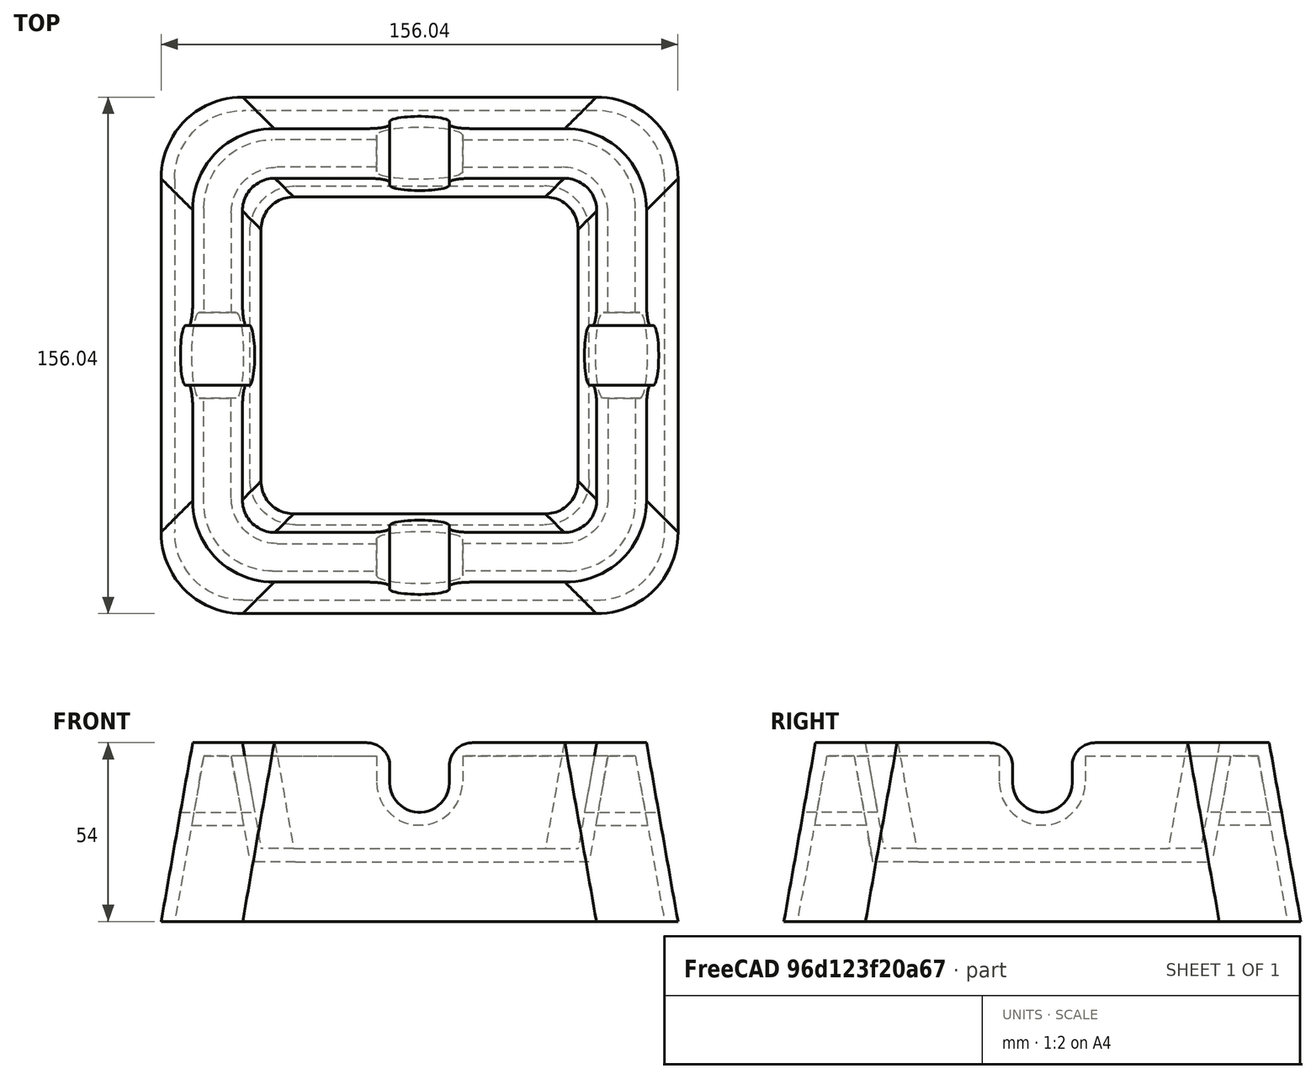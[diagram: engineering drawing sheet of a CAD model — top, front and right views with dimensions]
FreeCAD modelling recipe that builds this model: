
FCSTD DOCUMENT  (FreeCAD 1.1R42340 (Git))
Label: 25-SPO-22-BAD_IDEA
License: Creative Commons Attribution-NonCommercial-ShareAlike 4.0
LicenseURL: https://creativecommons.org/licenses/by-nc-sa/4.0/
objects: Sketcher::SketchObject×3, PartDesign::Fillet×3, PartDesign::Pocket×2, App::Point×1, PartDesign::Pad×1, PartDesign::PolarPattern×1, PartDesign::Thickness×1, PartDesign::Body×1, App::TextDocument×1
note: 30 computed .brp shape members not serialized (recipe doc carries the construction recipe); baked Part::Feature solids carry a one-line shape summary decoded from their .brp

FEATURE [App::Point] Origin001  label="Origine"
  Role = Origin
FEATURE [Sketcher::SketchObject] Sketch002
  ArcFitTolerance = 1e-06
  ExternalTypes = [0,0,0,0,0]
  FullyConstrained = true
  MakeInternals = false
  MapMode = 5
  Placement = pos=(0,0,0) rot=(1,0,0;3.14159rad)
  sketch-geometry (6):
    g0: LineSegment StartX=-68.5 StartY=68.5 StartZ=0 EndX=-68.5 EndY=-68.5 EndZ=0
    g1: LineSegment StartX=-68.5 StartY=-68.5 StartZ=0 EndX=68.5 EndY=-68.5 EndZ=0
    g2: LineSegment StartX=68.5 StartY=-68.5 StartZ=0 EndX=68.5 EndY=68.5 EndZ=0
    g3: LineSegment StartX=68.5 StartY=68.5 StartZ=0 EndX=-68.5 EndY=68.5 EndZ=0
    g4: GeomPoint [constr] X=-68.5 Y=68.5 Z=0
    g5: GeomPoint [constr] X=68.5 Y=-68.5 Z=0
  constraints (13):
    c: Vertical(g0)
    c: Vertical(g2)
    c: Horizontal(g1)
    c: Horizontal(g3)
    c: Equal(g2,g3)
    c: Coincident(g1,g2)
    c: Coincident(g1,g5)
    c: Coincident(g0,g3)
    c: Coincident(g0,g4)
    c: Coincident(g0,g1)
    c: Coincident(g2,g3)
    c: Symmetric(g0,g1,g-1)
    c: DistanceX(g1,g1) = 137
FEATURE [PartDesign::Pad] Pad
  Direction = (0,0,-1)
  Length = 54
  Length2 = 10
  Placement = pos=(0,0,0) rot=(1,0,0;3.14159rad)
  Profile = -> Sketch002
  ReferenceAxis = -> Sketch002 [N_Axis]
  Refine = true
  Suppressed = false
  TaperAngle = 10
  Type = 0
FEATURE [Sketcher::SketchObject] Sketch
  ArcFitTolerance = 1e-06
  AttachmentSupport = -> [Pad]
  ExternalGeometry = -> [Sketch002]
  ExternalTypes = [0,0]
  FullyConstrained = true
  MakeInternals = false
  MapMode = 5
  sketch-geometry (5):
    g0: LineSegment StartX=-53.5 StartY=-53.5 StartZ=0 EndX=-53.5 EndY=53.5 EndZ=0
    g1: LineSegment StartX=-53.5 StartY=53.5 StartZ=0 EndX=53.5 EndY=53.5 EndZ=0
    g2: LineSegment StartX=53.5 StartY=53.5 StartZ=0 EndX=53.5 EndY=-53.5 EndZ=0
    g3: LineSegment StartX=53.5 StartY=-53.5 StartZ=0 EndX=-53.5 EndY=-53.5 EndZ=0
    g4: LineSegment [constr] StartX=-53.5 StartY=53.5 StartZ=0 EndX=-53.5 EndY=68.5 EndZ=0
  constraints (15):
    c: Coincident(g0,g1)
    c: Coincident(g0,g3)
    c: Coincident(g1,g2)
    c: Coincident(g2,g3)
    c: Perpendicular(g4,g1)
    c: PointOnObject(g4,g1)
    c: Vertical(g4,g0)
    c: Horizontal(g3)
    c: Vertical(g0)
    c: Vertical(g2)
    c: PointOnObject(g4,g-3)
    c: Horizontal(g1)
    c: Equal(g0,g1)
    c: Symmetric(g2,g4,g-1)
    c: Distance(g4,g4) = 15
FEATURE [PartDesign::Pocket] Pocket
  BaseFeature = -> Pad
  Direction = (0,0,-1)
  Length = 32
  Length2 = 5
  Offset = -22
  Placement = pos=(0,0,0) rot=(1,0,0;3.14159rad)
  Profile = -> Sketch
  ReferenceAxis = -> Sketch [N_Axis]
  Refine = true
  Suppressed = false
  TaperAngle = -10
  Type = 0
  expr: Length = 54 - 22
FEATURE [Sketcher::SketchObject] Sketch003
  ArcFitTolerance = 1e-06
  AttachmentSupport = -> [Origin]
  ExternalTypes = [0]
  FullyConstrained = true
  MakeInternals = false
  MapMode = 5
  Placement = pos=(0,0,0) rot=(1,0,0;1.5708rad)
  sketch-geometry (4):
    g0: ArcOfCircle CenterX=0 CenterY=0 CenterZ=0 NormalX=0 NormalY=0 NormalZ=1 AngleXU=0 Radius=9 StartAngle=1e-16 EndAngle=3.14159
    g1: ArcOfCircle CenterX=-7e-16 CenterY=-12 CenterZ=0 NormalX=0 NormalY=0 NormalZ=1 AngleXU=0 Radius=9 StartAngle=3.14159 EndAngle=6.28319
    g2: LineSegment StartX=9 StartY=1.1e-15 StartZ=0 EndX=9 EndY=-12 EndZ=0
    g3: LineSegment StartX=-9 StartY=1.1e-15 StartZ=0 EndX=-9 EndY=-12 EndZ=0
  constraints (9):
    c: Tangent(g0,g2) = 1.5708
    c: Tangent(g0,g3) = -1.5708
    c: Tangent(g1,g2) = 1.5708
    c: Tangent(g1,g3) = -1.5708
    c: Equal(g0,g1)
    c: Vertical(g3)
    c: Radius(g0) = 9
    c: Coincident(g0,g-1)
    c: Distance(g1,g-1) = 12
FEATURE [PartDesign::Pocket] Pocket001
  BaseFeature = -> Pocket
  Direction = (0,1,-2e-16)
  Length = 5
  Length2 = 5
  Midplane = true
  Placement = pos=(0,0,0) rot=(1,0,0;3.14159rad)
  Profile = -> Sketch003
  ReferenceAxis = -> Sketch003 [N_Axis]
  Refine = true
  Suppressed = false
  Type = 1
FEATURE [PartDesign::PolarPattern] PolarPattern
  Angle = 90
  Axis = -> Z_Axis
  BaseFeature = -> Pocket001
  Mode = 1
  Occurrences = 2
  Offset = 90
  Originals = -> [Pocket001]
  Placement = pos=(0,0,0) rot=(1,0,0;3.14159rad)
  Refine = true
  Suppressed = false
  TransformMode = 0
FEATURE [PartDesign::Fillet] Fillet
  Base = -> PolarPattern [Edge65,Edge63,Edge60,Edge62]
  BaseFeature = -> PolarPattern
  Placement = pos=(0,0,0) rot=(1,0,0;3.14159rad)
  Radius = 10
  Refine = true
  SupportTransform = false
  Suppressed = false
  UseAllEdges = false
FEATURE [PartDesign::Fillet] Fillet001
  Base = -> Fillet [Edge59,Edge33,Edge25,Edge27]
  BaseFeature = -> Fillet
  Placement = pos=(0,0,0) rot=(1,0,0;3.14159rad)
  Radius = 25
  Refine = true
  SupportTransform = false
  Suppressed = false
  UseAllEdges = false
FEATURE [PartDesign::Thickness] Thickness
  Base = -> Fillet001 [Face10]
  BaseFeature = -> Fillet001
  Intersection = false
  Join = 1
  Mode = 0
  Refine = true
  Reversed = true
  SupportTransform = false
  Suppressed = false
  Value = 4
FEATURE [PartDesign::Fillet] Fillet002
  Base = -> Thickness [Edge55,Edge93,Edge6,Edge53,Edge3,Edge47,Edge45,Edge94]
  BaseFeature = -> Thickness
  Radius = 7
  Refine = true
  SupportTransform = false
  Suppressed = false
  UseAllEdges = false
FEATURE [PartDesign::Body] Body  label="Corps"
  AllowCompound = false
  Group = -> [Sketch002,Pad,Sketch,Pocket,Sketch003,Pocket001,PolarPattern,Fillet,Fillet001,Thickness,Fillet002]
  Origin = -> Origin
  Tip = -> Fillet002
FEATURE [App::TextDocument] Text_document  label="README"
  Text = https://www.youtube.com/watch?v=zMTYT-ui2u4\n\n1020 kg/m3\n\n213g ****************\n\nshould be 180g...
